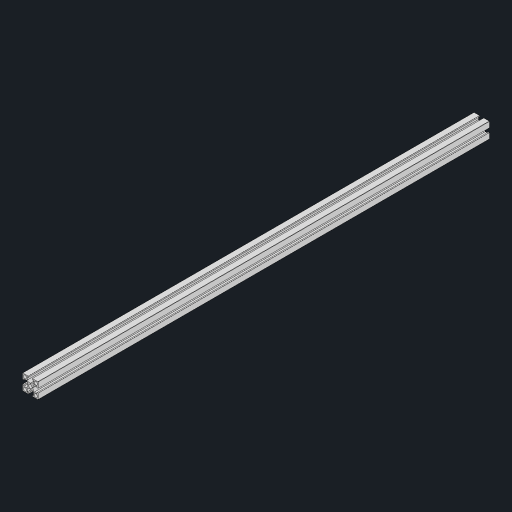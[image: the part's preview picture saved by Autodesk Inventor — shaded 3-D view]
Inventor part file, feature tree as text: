
AUTODESK INVENTOR PART (.ipt)
format: ipt  version: 2024.2 (Build 282272000, 272)  size: 234,496 bytes
history: native  units: mm
features: other x1, extrude x1, fillet x1, sketch x1
ambient origin geometry x8: Origin, YZ Plane, XZ Plane, XY Plane, X Axis, Y Axis, Z Axis, Center Point
bodies: Body1 (feature_tree)
feature tree (4):
  other  "솔리드1"
  extrude  "프로파일 길이 설정"  Depth=20.0mm
  fillet  "모서리"  Radius=20.0mm
  sketch  "스케치1"
